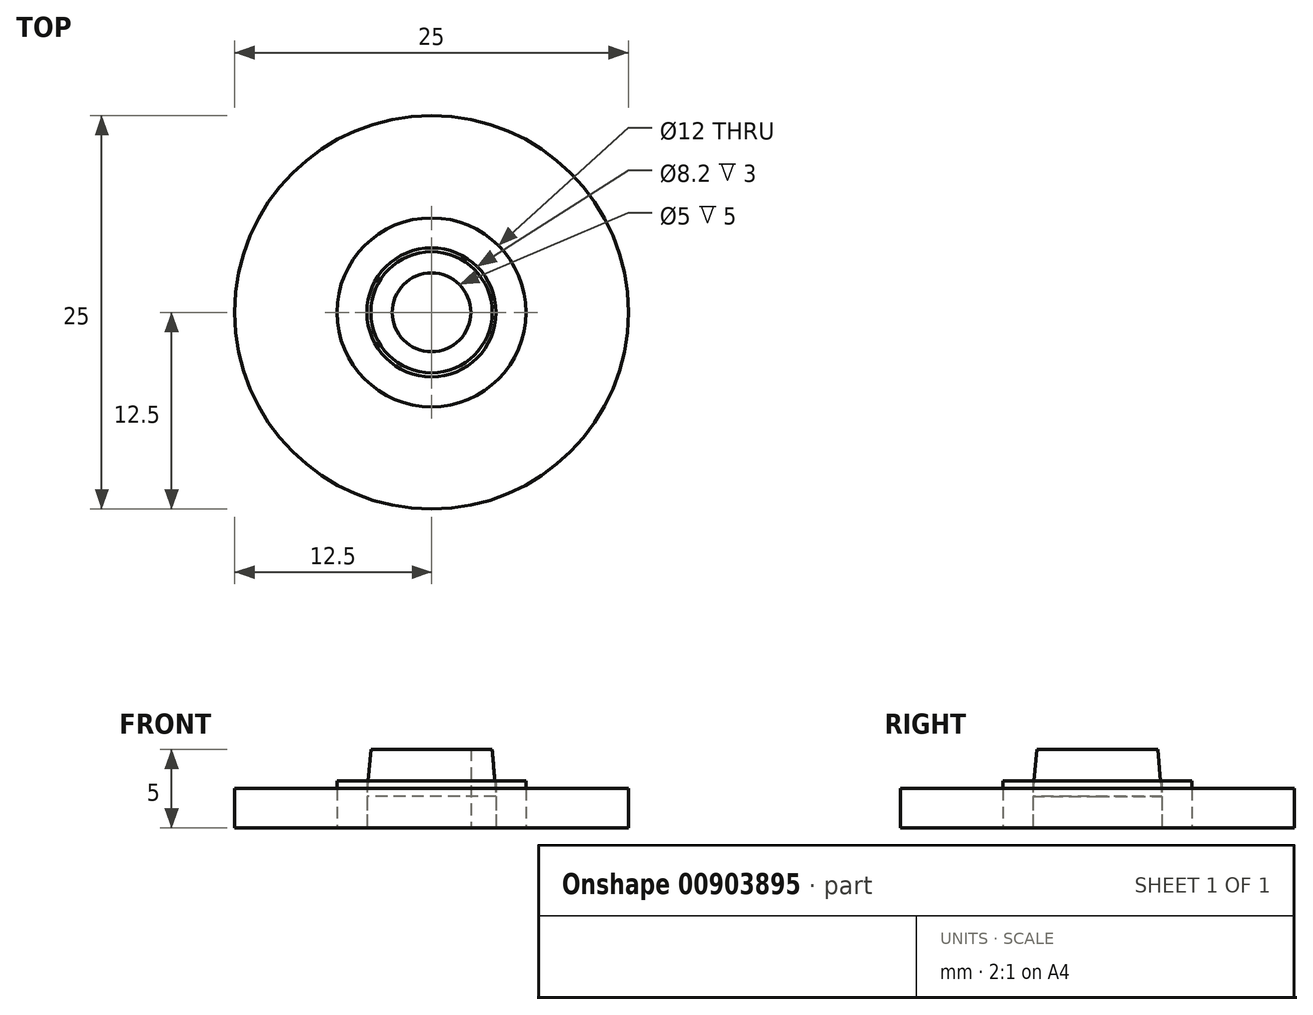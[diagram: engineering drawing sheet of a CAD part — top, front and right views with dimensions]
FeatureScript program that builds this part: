
annotation { "Feature Type Name" : "Feature", "Feature Type Description" : "" }
export const myFeature = defineFeature(function(context is Context, id is Id, definition is map)
    precondition{}
    {
        {
            var Q0;
            Q0=qCreatedBy(makeId("Top.planeOp"),FACE);
            var sketch = newSketch(context, id + "F0", { "sketchPlane" : qUnion([Q0])});
            skCircle(sketch, "E0", {"center": v(0, 0) * mm, "radius": 4.1 * mm});
            skCircle(sketch, "E1", {"center": v(0, 0) * mm, "radius": 12.5 * mm});
            skCircle(sketch, "E2", {"center": v(0, 0) * mm, "radius": 2.5 * mm});
            skCircle(sketch, "E3", {"center": v(0, 0) * mm, "radius": 6 * mm});
            skSolve(sketch);
        }
        {
            var Q0;
            Q0=makeQuery(id+"F0.imprint","IMPRINT",FACE,{"disambiguationData":[TD([[makeQuery(id+"F0.imprint","IMPRINT",EDGE,{"derivedFrom":sQuery(id+"F0.wireOp",EDGE,"E0")}),1.0]])]});
            extrude(context, id + "F1", {"entities" : qUnion([Q0]), "depth" : 5 * mm, "offsetDistance" : 25 * mm});
        }
        {
            var Q0;
            Q0 = qSketchRegion(id + "F0", true);
            extrude(context, id + "F2", {"entities" : qUnion([Q0]), "operationType" : NewBodyOperationType.ADD, "depth" : 2.5 * mm, "offsetDistance" : 25 * mm});
        }
        {
            var Q0;
            Q0=makeQuery(id+"F0.imprint","IMPRINT",FACE,{"disambiguationData":[TD([[makeQuery(id+"F0.imprint","IMPRINT",EDGE,{"derivedFrom":sQuery(id+"F0.wireOp",EDGE,"E0")}),-1.0]])]});
            extrude(context, id + "F3", {"entities" : qUnion([Q0]), "depth" : 3 * mm, "offsetDistance" : 25 * mm});
        }
        {
            var Q0;
            Q0=makeQuery(id+"F1.opExtrude","CAP_EDGE",EDGE,{"disambiguationData":[OSD([sQuery(id+"F0.wireOp",EDGE,"E0")])],"isStart":false});
            chamfer(context, id + "F4", {"entities" : qUnion([Q0]), "chamferType" : ChamferType.TWO_OFFSETS, "width1" : .25 * mm, "oppositeDirection" : false, "width2" : 3 * mm, "tangentPropagation" : true});
        }
    });
